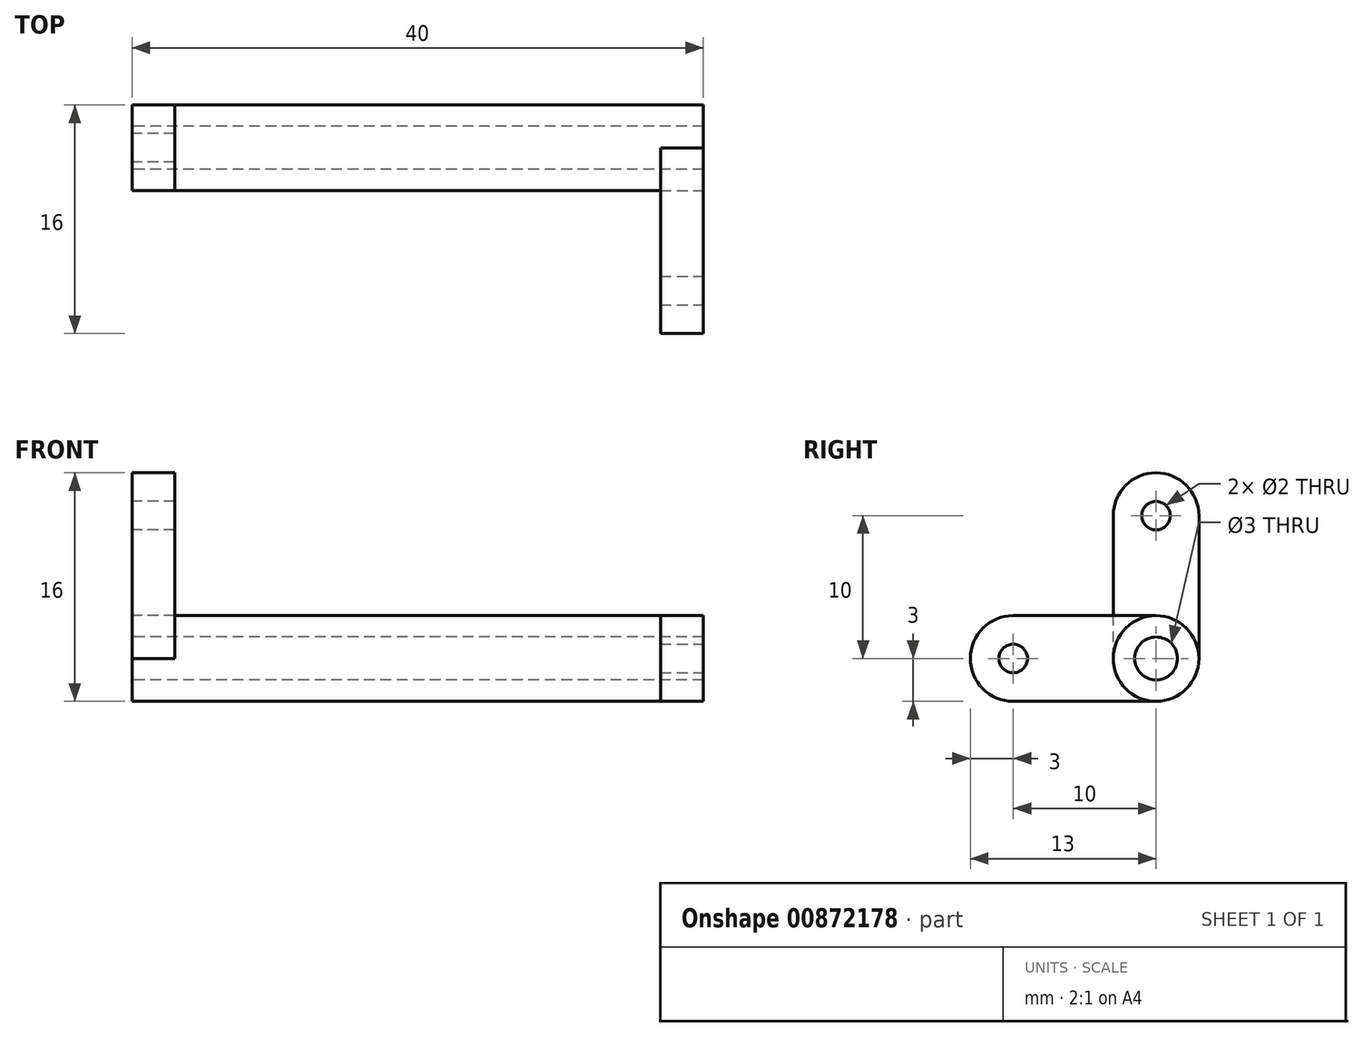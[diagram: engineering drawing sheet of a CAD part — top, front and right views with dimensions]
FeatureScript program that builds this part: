
annotation { "Feature Type Name" : "Feature", "Feature Type Description" : "" }
export const myFeature = defineFeature(function(context is Context, id is Id, definition is map)
    precondition{}
    {
        {
            var Q0;
            Q0=qCreatedBy(makeId("Right.planeOp"),FACE);
            var sketch = newSketch(context, id + "F0", { "sketchPlane" : qUnion([Q0])});
            skCircle(sketch, "E0", {"center": v(0, 0) * mm, "radius": 3 * mm});
            skCircle(sketch, "E1", {"center": v(0, 0) * mm, "radius": 1.5 * mm});
            skSolve(sketch);
        }
        {
            var Q0;
            Q0=makeQuery(id+"F0.imprint","IMPRINT",FACE,{"disambiguationData":[TD([[makeQuery(id+"F0.imprint","IMPRINT",EDGE,{"derivedFrom":sQuery(id+"F0.wireOp",EDGE,"E0")}),1.0]])]});
            extrude(context, id + "F1", {"entities" : qUnion([Q0]), "depth" : 40 * mm, "offsetDistance" : 25 * mm});
        }
        {
            var Q0;
            Q0=makeQuery(id+"F1.opExtrude","CAP_FACE",FACE,{"disambiguationData":[OSD([sQuery(id+"F0.wireOp",EDGE,"E0"),sQuery(id+"F0.wireOp",EDGE,"E1")])],"isStart":false});
            var sketch = newSketch(context, id + "F2", { "sketchPlane" : qUnion([Q0])});
            skLineSegment(sketch, "E2.bottom", {"start": v(0, -3) * mm, "end": v(-10, -3) * mm});
            skLineSegment(sketch, "E2.top", {"start": v(0, 3) * mm, "end": v(-10, 3) * mm});
            skLineSegment(sketch, "E2.left", {"start": v(0, -3) * mm, "end": v(0, 3) * mm});
            skLineSegment(sketch, "E2.right", {"start": v(-10, -3) * mm, "end": v(-10, 3) * mm});
            skCircle(sketch, "E3", {"center": v(-10, 0) * mm, "radius": 3 * mm});
            skCircle(sketch, "E4", {"center": v(-10, 0) * mm, "radius": 1 * mm});
            skSolve(sketch);
        }
        {
            var Q0;
            {var subQ0=sQuery(id+"F2.wireOp",EDGE,"E2.bottom");Q0=makeQuery(id+"F2.imprint","IMPRINT",FACE,{"disambiguationData":[TD([[makeQuery(id+"F2.imprint","IMPRINT",EDGE,{"derivedFrom":subQ0}),-1.0]])]});}
            var Q1;
            {var subQ1=sQuery(id+"F2.wireOp",EDGE,"E2.right");var subQ3=sQuery(id+"F2.wireOp",EDGE,"E4");var subQ4=makeQuery(id+"F2.imprint","INTERSECT",VERTEX,{"disambiguationData":[OD(0.0)],"derivedFrom":[subQ1,subQ3]});Q1=makeQuery(id+"F2.imprint","IMPRINT",FACE,{"disambiguationData":[TD([[makeQuery(id+"F2.imprint","IMPRINT",EDGE,{"disambiguationData":[TD([[subQ4,-1.0]])],"derivedFrom":subQ3}),-1.0]])]});}
            var Q2;
            {var subQ1=sQuery(id+"F2.wireOp",EDGE,"E2.right");var subQ3=sQuery(id+"F2.wireOp",EDGE,"E4");var subQ4=makeQuery(id+"F2.imprint","INTERSECT",VERTEX,{"disambiguationData":[OD(0.0)],"derivedFrom":[subQ1,subQ3]});Q2=makeQuery(id+"F2.imprint","IMPRINT",FACE,{"disambiguationData":[TD([[makeQuery(id+"F2.imprint","IMPRINT",EDGE,{"disambiguationData":[TD([[subQ4,1.0]])],"derivedFrom":subQ3}),-1.0]])]});}
            extrude(context, id + "F3", {"entities" : qUnion([Q0, Q1, Q2]), "oppositeDirection" : true, "depth" : 3 * mm, "offsetDistance" : 25 * mm});
        }
        {
            var Q0;
            Q0=makeQuery(id+"F1.opExtrude","CAP_FACE",FACE,{"disambiguationData":[OSD([sQuery(id+"F0.wireOp",EDGE,"E0"),sQuery(id+"F0.wireOp",EDGE,"E1")])],"isStart":true});
            var sketch = newSketch(context, id + "F4", { "sketchPlane" : qUnion([Q0])});
            skLineSegment(sketch, "E5.bottom", {"start": v(-3, 0) * mm, "end": v(3, 0) * mm});
            skLineSegment(sketch, "E5.top", {"start": v(-3, 10) * mm, "end": v(3, 10) * mm});
            skLineSegment(sketch, "E5.left", {"start": v(-3, 0) * mm, "end": v(-3, 10) * mm});
            skLineSegment(sketch, "E5.right", {"start": v(3, 0) * mm, "end": v(3, 10) * mm});
            skCircle(sketch, "E6", {"center": v(0, 10) * mm, "radius": 3 * mm});
            skCircle(sketch, "E7", {"center": v(0, 10) * mm, "radius": 1 * mm});
            skSolve(sketch);
        }
        {
            var Q0;
            {var subQ0=sQuery(id+"F4.wireOp",EDGE,"E5.left");Q0=makeQuery(id+"F4.imprint","IMPRINT",FACE,{"disambiguationData":[TD([[makeQuery(id+"F4.imprint","IMPRINT",EDGE,{"derivedFrom":subQ0}),-1.0]])]});}
            var Q1;
            {var subQ1=sQuery(id+"F4.wireOp",EDGE,"E5.top");var subQ3=sQuery(id+"F4.wireOp",EDGE,"E7");var subQ4=makeQuery(id+"F4.imprint","INTERSECT",VERTEX,{"disambiguationData":[OD(0.0)],"derivedFrom":[subQ1,subQ3]});Q1=makeQuery(id+"F4.imprint","IMPRINT",FACE,{"disambiguationData":[TD([[makeQuery(id+"F4.imprint","IMPRINT",EDGE,{"disambiguationData":[TD([[subQ4,-1.0]])],"derivedFrom":subQ3}),-1.0]])]});}
            var Q2;
            {var subQ1=sQuery(id+"F4.wireOp",EDGE,"E5.top");var subQ3=sQuery(id+"F4.wireOp",EDGE,"E7");var subQ4=makeQuery(id+"F4.imprint","INTERSECT",VERTEX,{"disambiguationData":[OD(0.0)],"derivedFrom":[subQ1,subQ3]});Q2=makeQuery(id+"F4.imprint","IMPRINT",FACE,{"disambiguationData":[TD([[makeQuery(id+"F4.imprint","IMPRINT",EDGE,{"disambiguationData":[TD([[subQ4,1.0]])],"derivedFrom":subQ3}),-1.0]])]});}
            extrude(context, id + "F5", {"entities" : qUnion([Q0, Q1, Q2]), "oppositeDirection" : true, "depth" : 3 * mm, "offsetDistance" : 25 * mm});
        }
    });
